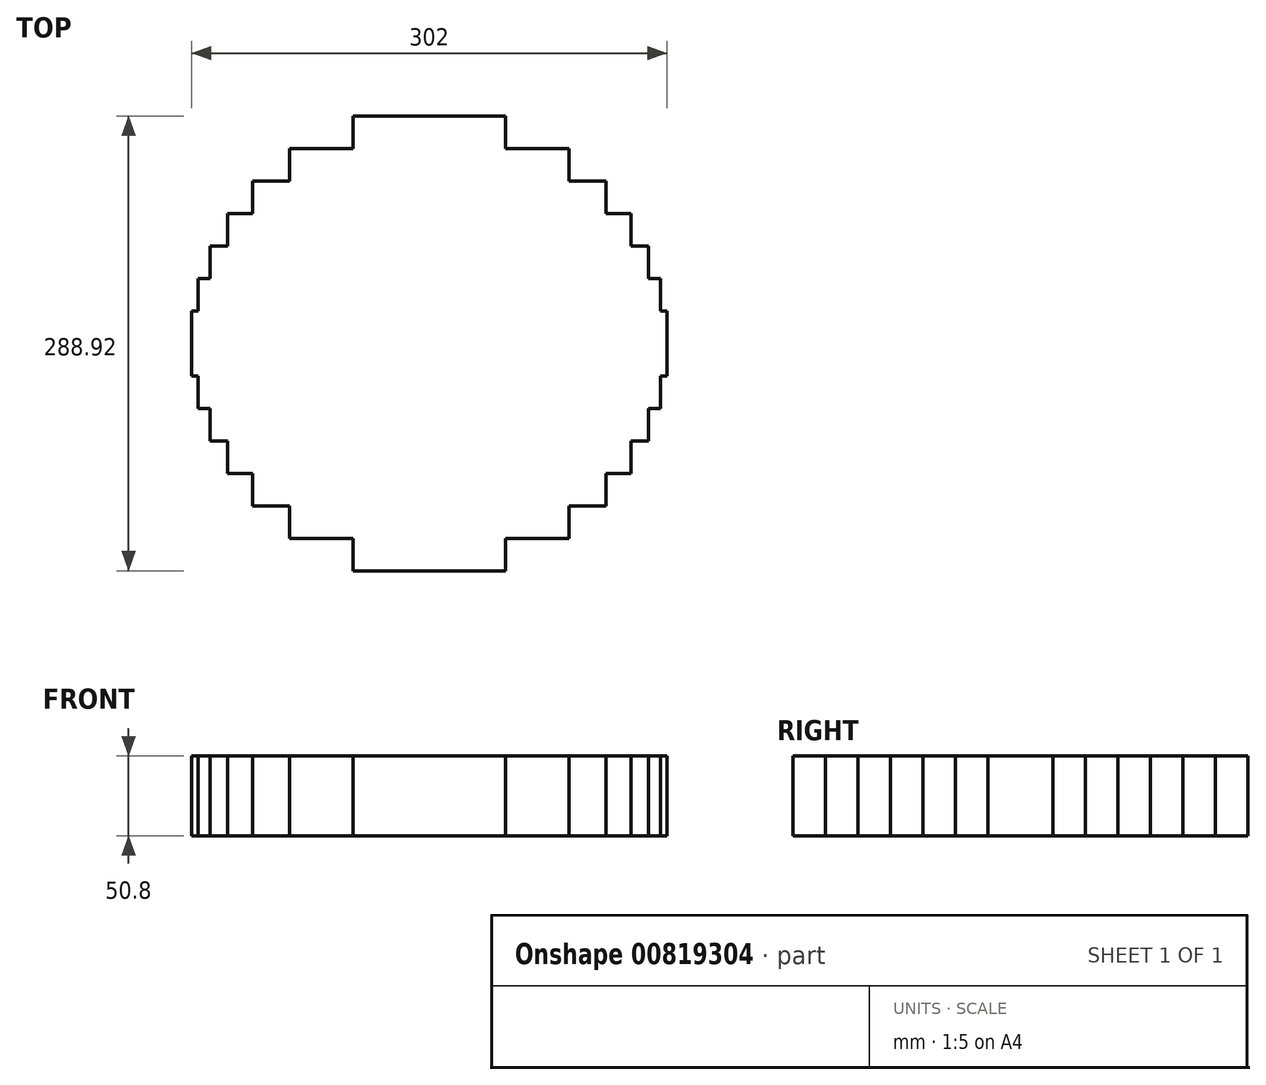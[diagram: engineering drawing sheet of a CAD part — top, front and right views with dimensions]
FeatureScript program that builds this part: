
annotation { "Feature Type Name" : "Feature", "Feature Type Description" : "" }
export const myFeature = defineFeature(function(context is Context, id is Id, definition is map)
    precondition{}
    {
        {
            var Q0;
            Q0=qCreatedBy(makeId("Top.planeOp"),FACE);
            var sketch = newSketch(context, id + "F0", { "sketchPlane" : qUnion([Q0])});
            skCircle(sketch, "E0", {"center": v(0, 0) * mm, "radius": 152.4 * mm, "construction": true});
            skLineSegment(sketch, "E1", {"start": v(0, -152.4) * mm, "end": v(0, 152.4) * mm, "construction": true});
            skLineSegment(sketch, "E2", {"start": v(-152.4, 0) * mm, "end": v(152.4, 0) * mm, "construction": true});
            skLineSegment(sketch, "E3.bottom", {"start": v(-31.47, 0) * mm, "end": v(151, 0) * mm});
            skLineSegment(sketch, "E3.top", {"start": v(-31.47, -20.64) * mm, "end": v(151, -20.64) * mm});
            skLineSegment(sketch, "E3.left", {"start": v(-31.47, 0) * mm, "end": v(-31.47, -20.64) * mm});
            skLineSegment(sketch, "E3.right", {"start": v(151, 0) * mm, "end": v(151, -20.64) * mm});
            skLineSegment(sketch, "E4.bottom", {"start": v(-31.47, 0) * mm, "end": v(-151, 0) * mm});
            skLineSegment(sketch, "E4.top", {"start": v(-31.47, -20.64) * mm, "end": v(-151, -20.64) * mm});
            skLineSegment(sketch, "E4.right", {"start": v(-151, 0) * mm, "end": v(-151, -20.64) * mm});
            skLineSegment(sketch, "E5.bottom", {"start": v(22.18, -20.64) * mm, "end": v(146.7, -20.64) * mm});
            skLineSegment(sketch, "E5.top", {"start": v(22.18, -41.27) * mm, "end": v(146.7, -41.27) * mm});
            skLineSegment(sketch, "E5.left", {"start": v(22.18, -20.64) * mm, "end": v(22.18, -41.27) * mm});
            skLineSegment(sketch, "E5.right", {"start": v(146.7, -20.64) * mm, "end": v(146.7, -41.27) * mm});
            skLineSegment(sketch, "E6.bottom", {"start": v(22.18, -20.64) * mm, "end": v(-146.7, -20.64) * mm});
            skLineSegment(sketch, "E6.top", {"start": v(22.18, -41.27) * mm, "end": v(-146.7, -41.27) * mm});
            skLineSegment(sketch, "E6.right", {"start": v(-146.7, -20.64) * mm, "end": v(-146.7, -41.27) * mm});
            skLineSegment(sketch, "E7.bottom", {"start": v(-70.1, -41.27) * mm, "end": v(139.26, -41.27) * mm});
            skLineSegment(sketch, "E7.top", {"start": v(-70.1, -61.91) * mm, "end": v(139.26, -61.91) * mm});
            skLineSegment(sketch, "E7.left", {"start": v(-70.1, -41.27) * mm, "end": v(-70.1, -61.91) * mm});
            skLineSegment(sketch, "E7.right", {"start": v(139.26, -41.27) * mm, "end": v(139.26, -61.91) * mm});
            skLineSegment(sketch, "E8.bottom", {"start": v(-70.1, -41.27) * mm, "end": v(-139.26, -41.27) * mm});
            skLineSegment(sketch, "E8.top", {"start": v(-70.1, -61.91) * mm, "end": v(-139.26, -61.91) * mm});
            skLineSegment(sketch, "E8.right", {"start": v(-139.26, -41.27) * mm, "end": v(-139.26, -61.91) * mm});
            skLineSegment(sketch, "E9.bottom", {"start": v(96.62, -61.91) * mm, "end": v(128.1, -61.91) * mm});
            skLineSegment(sketch, "E9.top", {"start": v(96.62, -82.55) * mm, "end": v(128.1, -82.55) * mm});
            skLineSegment(sketch, "E9.left", {"start": v(96.62, -61.91) * mm, "end": v(96.62, -82.55) * mm});
            skLineSegment(sketch, "E9.right", {"start": v(128.1, -61.91) * mm, "end": v(128.1, -82.55) * mm});
            skLineSegment(sketch, "E10.bottom", {"start": v(96.62, -82.55) * mm, "end": v(-32.87, -82.55) * mm});
            skLineSegment(sketch, "E10.top", {"start": v(96.62, -61.91) * mm, "end": v(-32.87, -61.91) * mm});
            skLineSegment(sketch, "E10.left", {"start": v(96.62, -82.55) * mm, "end": v(96.62, -61.91) * mm});
            skLineSegment(sketch, "E10.right", {"start": v(-32.87, -82.55) * mm, "end": v(-32.87, -61.91) * mm});
            skLineSegment(sketch, "E11.bottom", {"start": v(-32.87, -61.91) * mm, "end": v(-128.1, -61.91) * mm});
            skLineSegment(sketch, "E11.top", {"start": v(-32.87, -82.55) * mm, "end": v(-128.1, -82.55) * mm});
            skLineSegment(sketch, "E11.left", {"start": v(-32.87, -61.91) * mm, "end": v(-32.87, -82.55) * mm});
            skLineSegment(sketch, "E11.right", {"start": v(-128.1, -61.91) * mm, "end": v(-128.1, -82.55) * mm});
            skLineSegment(sketch, "E12.bottom", {"start": v(-112.15, -82.55) * mm, "end": v(55.9, -82.55) * mm});
            skLineSegment(sketch, "E12.top", {"start": v(-112.15, -103.19) * mm, "end": v(55.9, -103.19) * mm});
            skLineSegment(sketch, "E12.left", {"start": v(-112.15, -82.55) * mm, "end": v(-112.15, -103.19) * mm});
            skLineSegment(sketch, "E12.right", {"start": v(55.9, -82.55) * mm, "end": v(55.9, -103.19) * mm});
            skLineSegment(sketch, "E13.bottom", {"start": v(55.9, -82.55) * mm, "end": v(112.15, -82.55) * mm});
            skLineSegment(sketch, "E13.top", {"start": v(55.9, -103.19) * mm, "end": v(112.15, -103.19) * mm});
            skLineSegment(sketch, "E13.right", {"start": v(112.15, -82.55) * mm, "end": v(112.15, -103.19) * mm});
            skLineSegment(sketch, "E14.bottom", {"start": v(88.84, -103.19) * mm, "end": v(-88.84, -103.19) * mm});
            skLineSegment(sketch, "E14.top", {"start": v(88.84, -123.82) * mm, "end": v(-88.84, -123.82) * mm});
            skLineSegment(sketch, "E14.left", {"start": v(88.84, -103.19) * mm, "end": v(88.84, -123.82) * mm});
            skLineSegment(sketch, "E14.right", {"start": v(-88.84, -103.19) * mm, "end": v(-88.84, -123.82) * mm});
            skLineSegment(sketch, "E15.bottom", {"start": v(34.6, -123.82) * mm, "end": v(-48.54, -123.82) * mm});
            skLineSegment(sketch, "E15.top", {"start": v(34.6, -144.46) * mm, "end": v(-48.54, -144.46) * mm});
            skLineSegment(sketch, "E15.left", {"start": v(34.6, -123.82) * mm, "end": v(34.6, -144.46) * mm});
            skLineSegment(sketch, "E15.right", {"start": v(-48.54, -123.82) * mm, "end": v(-48.54, -144.46) * mm});
            skLineSegment(sketch, "E16.bottom", {"start": v(34.6, -123.82) * mm, "end": v(48.54, -123.82) * mm});
            skLineSegment(sketch, "E16.top", {"start": v(34.6, -144.46) * mm, "end": v(48.54, -144.46) * mm});
            skLineSegment(sketch, "E16.right", {"start": v(48.54, -123.82) * mm, "end": v(48.54, -144.46) * mm});
            skLineSegment(sketch, "E17.1.0", {"start": v(31.47, 20.64) * mm, "end": v(151, 20.64) * mm});
            skLineSegment(sketch, "E17.1.1", {"start": v(-22.18, 41.27) * mm, "end": v(-146.7, 41.27) * mm});
            skLineSegment(sketch, "E17.1.2", {"start": v(-22.18, 20.64) * mm, "end": v(-146.7, 20.64) * mm});
            skLineSegment(sketch, "E17.1.3", {"start": v(70.1, 61.91) * mm, "end": v(139.26, 61.91) * mm});
            skLineSegment(sketch, "E17.1.4", {"start": v(70.1, 61.91) * mm, "end": v(-139.26, 61.91) * mm});
            skLineSegment(sketch, "E17.1.5", {"start": v(112.15, 103.19) * mm, "end": v(-55.9, 103.19) * mm});
            skLineSegment(sketch, "E17.1.6", {"start": v(-55.9, 103.19) * mm, "end": v(-112.15, 103.19) * mm});
            skLineSegment(sketch, "E17.1.7", {"start": v(-34.6, 144.46) * mm, "end": v(48.54, 144.46) * mm});
            skLineSegment(sketch, "E17.1.8", {"start": v(-22.18, 20.64) * mm, "end": v(-22.18, 41.27) * mm});
            skLineSegment(sketch, "E17.1.9", {"start": v(32.87, 82.55) * mm, "end": v(128.1, 82.55) * mm});
            skLineSegment(sketch, "E17.1.10", {"start": v(-22.18, 41.27) * mm, "end": v(146.7, 41.27) * mm});
            skLineSegment(sketch, "E17.1.11", {"start": v(-88.84, 123.82) * mm, "end": v(88.84, 123.82) * mm});
            skLineSegment(sketch, "E17.1.12", {"start": v(-96.62, 61.91) * mm, "end": v(32.87, 61.91) * mm});
            skLineSegment(sketch, "E17.1.13", {"start": v(31.47, 20.64) * mm, "end": v(-151, 20.64) * mm});
            skLineSegment(sketch, "E17.1.14", {"start": v(152.4, 0) * mm, "end": v(-152.4, 0) * mm, "construction": true});
            skLineSegment(sketch, "E17.1.15", {"start": v(-146.7, 20.64) * mm, "end": v(-146.7, 41.27) * mm});
            skLineSegment(sketch, "E17.1.16", {"start": v(-88.84, 103.19) * mm, "end": v(88.84, 103.19) * mm});
            skLineSegment(sketch, "E17.1.17", {"start": v(-96.62, 82.55) * mm, "end": v(32.87, 82.55) * mm});
            skLineSegment(sketch, "E17.1.18", {"start": v(146.7, 20.64) * mm, "end": v(146.7, 41.27) * mm});
            skLineSegment(sketch, "E17.1.19", {"start": v(-96.62, 61.91) * mm, "end": v(-128.1, 61.91) * mm});
            skLineSegment(sketch, "E17.1.20", {"start": v(-55.9, 82.55) * mm, "end": v(-112.15, 82.55) * mm});
            skLineSegment(sketch, "E17.1.21", {"start": v(70.1, 41.27) * mm, "end": v(139.26, 41.27) * mm});
            skLineSegment(sketch, "E17.1.22", {"start": v(112.15, 82.55) * mm, "end": v(-55.9, 82.55) * mm});
            skLineSegment(sketch, "E17.1.23", {"start": v(31.47, 0) * mm, "end": v(151, 0) * mm});
            skLineSegment(sketch, "E17.1.24", {"start": v(31.47, 0) * mm, "end": v(-151, 0) * mm});
            skLineSegment(sketch, "E17.1.25", {"start": v(-22.18, 20.64) * mm, "end": v(146.7, 20.64) * mm});
            skLineSegment(sketch, "E17.1.26", {"start": v(-22.18, 20.64) * mm, "end": v(-22.18, 41.27) * mm});
            skLineSegment(sketch, "E17.1.27", {"start": v(32.87, 61.91) * mm, "end": v(128.1, 61.91) * mm});
            skLineSegment(sketch, "E17.1.28", {"start": v(-34.6, 123.82) * mm, "end": v(48.54, 123.82) * mm});
            skLineSegment(sketch, "E17.1.29", {"start": v(70.1, 41.27) * mm, "end": v(-139.26, 41.27) * mm});
            skLineSegment(sketch, "E17.1.30", {"start": v(-34.6, 123.82) * mm, "end": v(-48.54, 123.82) * mm});
            skLineSegment(sketch, "E17.1.31", {"start": v(151, 0) * mm, "end": v(151, 20.64) * mm});
            skLineSegment(sketch, "E17.1.32", {"start": v(-112.15, 82.55) * mm, "end": v(-112.15, 103.19) * mm});
            skLineSegment(sketch, "E17.1.33", {"start": v(-34.6, 144.46) * mm, "end": v(-48.54, 144.46) * mm});
            skLineSegment(sketch, "E17.1.34", {"start": v(-96.62, 82.55) * mm, "end": v(-128.1, 82.55) * mm});
            skLineSegment(sketch, "E17.1.35", {"start": v(-151, 0) * mm, "end": v(-151, 20.64) * mm});
            skLineSegment(sketch, "E17.1.36", {"start": v(-128.1, 61.91) * mm, "end": v(-128.1, 82.55) * mm});
            skLineSegment(sketch, "E17.1.37", {"start": v(-88.84, 103.19) * mm, "end": v(-88.84, 123.82) * mm});
            skLineSegment(sketch, "E17.1.38", {"start": v(112.15, 82.55) * mm, "end": v(112.15, 103.19) * mm});
            skLineSegment(sketch, "E17.1.39", {"start": v(-139.26, 41.27) * mm, "end": v(-139.26, 61.91) * mm});
            skLineSegment(sketch, "E17.1.40", {"start": v(48.54, 123.82) * mm, "end": v(48.54, 144.46) * mm});
            skLineSegment(sketch, "E17.1.41", {"start": v(128.1, 61.91) * mm, "end": v(128.1, 82.55) * mm});
            skLineSegment(sketch, "E17.1.42", {"start": v(88.84, 103.19) * mm, "end": v(88.84, 123.82) * mm});
            skLineSegment(sketch, "E17.1.43", {"start": v(139.26, 41.27) * mm, "end": v(139.26, 61.91) * mm});
            skLineSegment(sketch, "E17.1.44", {"start": v(-48.54, 123.82) * mm, "end": v(-48.54, 144.46) * mm});
            skLineSegment(sketch, "E17.1.45", {"start": v(-55.9, 82.55) * mm, "end": v(-55.9, 103.19) * mm});
            skLineSegment(sketch, "E17.1.46", {"start": v(31.47, 0) * mm, "end": v(31.47, 20.64) * mm});
            skLineSegment(sketch, "E17.1.47", {"start": v(-96.62, 82.55) * mm, "end": v(-96.62, 61.91) * mm});
            skLineSegment(sketch, "E17.1.48", {"start": v(-34.6, 123.82) * mm, "end": v(-34.6, 144.46) * mm});
            skLineSegment(sketch, "E17.1.49", {"start": v(70.1, 41.27) * mm, "end": v(70.1, 61.91) * mm});
            skLineSegment(sketch, "E17.1.50", {"start": v(32.87, 82.55) * mm, "end": v(32.87, 61.91) * mm});
            skLineSegment(sketch, "E17.1.51", {"start": v(32.87, 61.91) * mm, "end": v(32.87, 82.55) * mm});
            skLineSegment(sketch, "E17.1.52", {"start": v(70.1, 41.27) * mm, "end": v(70.1, 61.91) * mm});
            skLineSegment(sketch, "E17.1.53", {"start": v(-34.6, 123.82) * mm, "end": v(-34.6, 144.46) * mm});
            skLineSegment(sketch, "E17.1.54", {"start": v(-96.62, 61.91) * mm, "end": v(-96.62, 82.55) * mm});
            skLineSegment(sketch, "E17.1.55", {"start": v(31.47, 0) * mm, "end": v(31.47, 20.64) * mm});
            skLineSegment(sketch, "E17.1.56", {"start": v(-55.9, 82.55) * mm, "end": v(-55.9, 103.19) * mm});
            skLineSegment(sketch, "E18.bottom", {"start": v(-32.87, -61.91) * mm, "end": v(96.62, -61.91) * mm});
            skLineSegment(sketch, "E18.top", {"start": v(-32.87, -82.55) * mm, "end": v(96.62, -82.55) * mm});
            skSolve(sketch);
        }
        {
            var Q0;
            Q0 = qSketchRegion(id + "F0", true);
            extrude(context, id + "F1", {"entities" : qUnion([Q0]), "depth" : 50.8 * mm, "offsetDistance" : 25.4 * mm});
        }
        {
            var Q0;
            Q0=makeQuery(id+"F1.opExtrude","CAP_FACE",FACE,{"disambiguationData":[OSD([sQuery(id+"F0.wireOp",EDGE,"E3.top"),sQuery(id+"F0.wireOp",EDGE,"E3.right"),sQuery(id+"F0.wireOp",EDGE,"E4.top"),sQuery(id+"F0.wireOp",EDGE,"E4.right"),sQuery(id+"F0.wireOp",EDGE,"E5.top"),sQuery(id+"F0.wireOp",EDGE,"E5.right"),sQuery(id+"F0.wireOp",EDGE,"E6.top"),sQuery(id+"F0.wireOp",EDGE,"E6.right"),sQuery(id+"F0.wireOp",EDGE,"E7.top"),sQuery(id+"F0.wireOp",EDGE,"E7.right"),sQuery(id+"F0.wireOp",EDGE,"E8.top"),sQuery(id+"F0.wireOp",EDGE,"E8.right"),sQuery(id+"F0.wireOp",EDGE,"E9.top"),sQuery(id+"F0.wireOp",EDGE,"E9.right"),sQuery(id+"F0.wireOp",EDGE,"E11.top"),sQuery(id+"F0.wireOp",EDGE,"E11.right"),sQuery(id+"F0.wireOp",EDGE,"E12.top"),sQuery(id+"F0.wireOp",EDGE,"E12.left"),sQuery(id+"F0.wireOp",EDGE,"E13.top"),sQuery(id+"F0.wireOp",EDGE,"E13.right"),sQuery(id+"F0.wireOp",EDGE,"E14.top"),sQuery(id+"F0.wireOp",EDGE,"E14.left"),sQuery(id+"F0.wireOp",EDGE,"E14.right"),sQuery(id+"F0.wireOp",EDGE,"E15.top"),sQuery(id+"F0.wireOp",EDGE,"E15.right"),sQuery(id+"F0.wireOp",EDGE,"E16.top"),sQuery(id+"F0.wireOp",EDGE,"E16.right"),sQuery(id+"F0.wireOp",EDGE,"E17.1.0"),sQuery(id+"F0.wireOp",EDGE,"E17.1.1"),sQuery(id+"F0.wireOp",EDGE,"E17.1.3"),sQuery(id+"F0.wireOp",EDGE,"E17.1.4"),sQuery(id+"F0.wireOp",EDGE,"E17.1.5"),sQuery(id+"F0.wireOp",EDGE,"E17.1.6"),sQuery(id+"F0.wireOp",EDGE,"E17.1.7"),sQuery(id+"F0.wireOp",EDGE,"E17.1.9"),sQuery(id+"F0.wireOp",EDGE,"E17.1.10"),sQuery(id+"F0.wireOp",EDGE,"E17.1.11"),sQuery(id+"F0.wireOp",EDGE,"E17.1.12"),sQuery(id+"F0.wireOp",EDGE,"E17.1.13"),sQuery(id+"F0.wireOp",EDGE,"E17.1.15"),sQuery(id+"F0.wireOp",EDGE,"E17.1.18"),sQuery(id+"F0.wireOp",EDGE,"E17.1.20"),sQuery(id+"F0.wireOp",EDGE,"E17.1.22"),sQuery(id+"F0.wireOp",EDGE,"E17.1.31"),sQuery(id+"F0.wireOp",EDGE,"E17.1.32"),sQuery(id+"F0.wireOp",EDGE,"E17.1.33"),sQuery(id+"F0.wireOp",EDGE,"E17.1.34"),sQuery(id+"F0.wireOp",EDGE,"E17.1.35"),sQuery(id+"F0.wireOp",EDGE,"E17.1.36"),sQuery(id+"F0.wireOp",EDGE,"E17.1.37"),sQuery(id+"F0.wireOp",EDGE,"E17.1.38"),sQuery(id+"F0.wireOp",EDGE,"E17.1.39"),sQuery(id+"F0.wireOp",EDGE,"E17.1.40"),sQuery(id+"F0.wireOp",EDGE,"E17.1.41"),sQuery(id+"F0.wireOp",EDGE,"E17.1.42"),sQuery(id+"F0.wireOp",EDGE,"E17.1.43"),sQuery(id+"F0.wireOp",EDGE,"E17.1.44"),sQuery(id+"F0.wireOp",EDGE,"E17.1.51"),sQuery(id+"F0.wireOp",EDGE,"E17.1.54"),sQuery(id+"F0.wireOp",EDGE,"E18.bottom"),sQuery(id+"F0.wireOp",EDGE,"E18.top"),sQuery(id+"F0.wireOp",EDGE,"E11.left"),sQuery(id+"F0.wireOp",EDGE,"E9.left")])],"isStart":false});
            var sketch = newSketch(context, id + "F2", { "sketchPlane" : qUnion([Q0])});
            skLineSegment(sketch, "E19.bottom", {"start": v(-32.87, -61.91) * mm, "end": v(96.62, -61.91) * mm});
            skLineSegment(sketch, "E19.top", {"start": v(-32.87, -82.55) * mm, "end": v(96.62, -82.55) * mm});
            skLineSegment(sketch, "E19.left", {"start": v(-32.87, -61.91) * mm, "end": v(-32.87, -82.55) * mm});
            skLineSegment(sketch, "E19.right", {"start": v(96.62, -61.91) * mm, "end": v(96.62, -82.55) * mm});
            skLineSegment(sketch, "E20.bottom", {"start": v(-96.62, 61.91) * mm, "end": v(32.87, 61.91) * mm});
            skLineSegment(sketch, "E20.top", {"start": v(-96.62, 82.55) * mm, "end": v(32.87, 82.55) * mm});
            skLineSegment(sketch, "E20.left", {"start": v(-96.62, 61.91) * mm, "end": v(-96.62, 82.55) * mm});
            skLineSegment(sketch, "E20.right", {"start": v(32.87, 61.91) * mm, "end": v(32.87, 82.55) * mm});
            skSolve(sketch);
        }
        {
            var Q0;
            Q0 = qSketchRegion(id + "F2", true);
            extrude(context, id + "F3", {"entities" : qUnion([Q0]), "operationType" : NewBodyOperationType.ADD, "oppositeDirection" : true, "depth" : 50.8 * mm, "offsetDistance" : 25.4 * mm});
        }
    });
